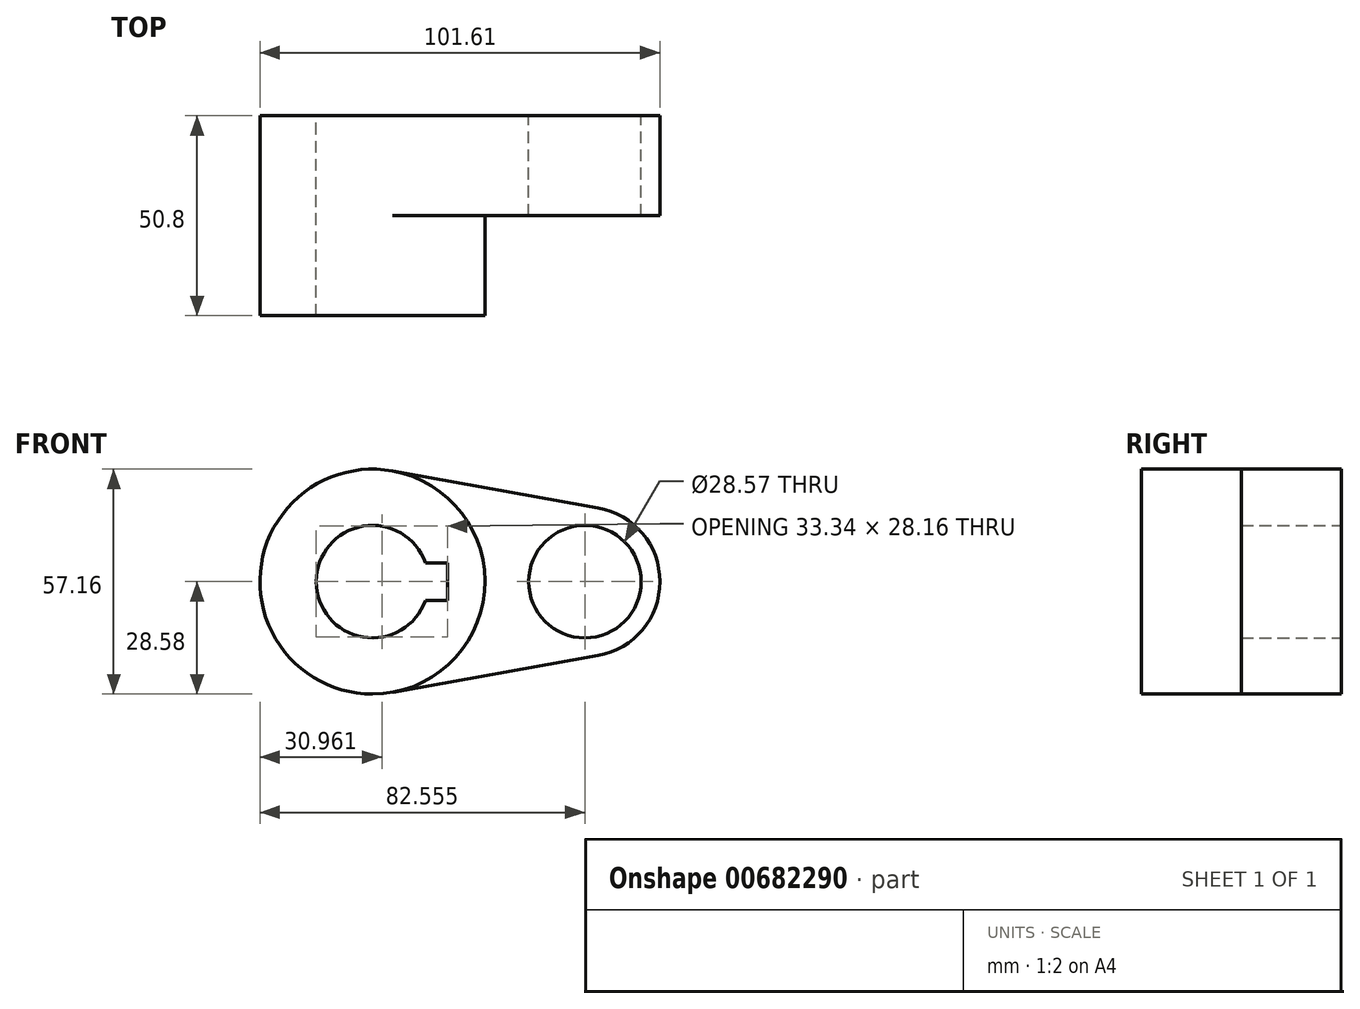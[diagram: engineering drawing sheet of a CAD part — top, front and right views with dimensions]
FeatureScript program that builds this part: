
annotation { "Feature Type Name" : "Feature", "Feature Type Description" : "" }
export const myFeature = defineFeature(function(context is Context, id is Id, definition is map)
    precondition{}
    {
        {
            var Q0;
            Q0=qCreatedBy(makeId("Front.planeOp"),FACE);
            var sketch = newSketch(context, id + "F0", { "sketchPlane" : qUnion([Q0])});
            skCircle(sketch, "E0", {"center": v(0, 0) * mm, "radius": 28.58 * mm});
            skCircle(sketch, "E1", {"center": v(53.97, 0) * mm, "radius": 19.05 * mm});
            skLineSegment(sketch, "E2", {"start": v(5.04, 28.13) * mm, "end": v(57.34, 18.75) * mm});
            skLineSegment(sketch, "E3", {"start": v(5.04, -28.13) * mm, "end": v(57.34, -18.75) * mm});
            skCircle(sketch, "E4", {"center": v(0, 0) * mm, "radius": 14.29 * mm});
            skCircle(sketch, "E5", {"center": v(53.97, 0) * mm, "radius": 14.29 * mm});
            skLineSegment(sketch, "E6.bottom", {"start": v(-19.05, 4.76) * mm, "end": v(19.05, 4.76) * mm});
            skLineSegment(sketch, "E6.top", {"start": v(-19.05, -4.76) * mm, "end": v(19.05, -4.76) * mm});
            skLineSegment(sketch, "E6.left", {"start": v(-19.05, 4.76) * mm, "end": v(-19.05, -4.76) * mm});
            skLineSegment(sketch, "E6.right", {"start": v(19.05, 4.76) * mm, "end": v(19.05, -4.76) * mm});
            skSolve(sketch);
        }
        {
            var Q0;
            {var subQ7=sQuery(id+"F0.wireOp",EDGE,"E6.left");Q0=makeQuery(id+"F0.imprint","IMPRINT",FACE,{"disambiguationData":[TD([[makeQuery(id+"F0.imprint","IMPRINT",EDGE,{"derivedFrom":subQ7}),-1.0]])]});}
            var Q1;
            {var subQ5=sQuery(id+"F0.wireOp",EDGE,"E6.left");Q1=makeQuery(id+"F0.imprint","IMPRINT",FACE,{"disambiguationData":[TD([[makeQuery(id+"F0.imprint","IMPRINT",EDGE,{"derivedFrom":subQ5}),1.0]])]});}
            extrude(context, id + "F1", {"entities" : qUnion([Q0, Q1]), "depth" : 50.8 * mm, "offsetDistance" : 25.4 * mm});
        }
        {
            var Q0;
            Q0 = qSketchRegion(id + "F0", true);
            extrude(context, id + "F2", {"entities" : qUnion([Q0]), "operationType" : NewBodyOperationType.ADD, "depth" : 25.4 * mm, "offsetDistance" : 25.4 * mm});
        }
    });
